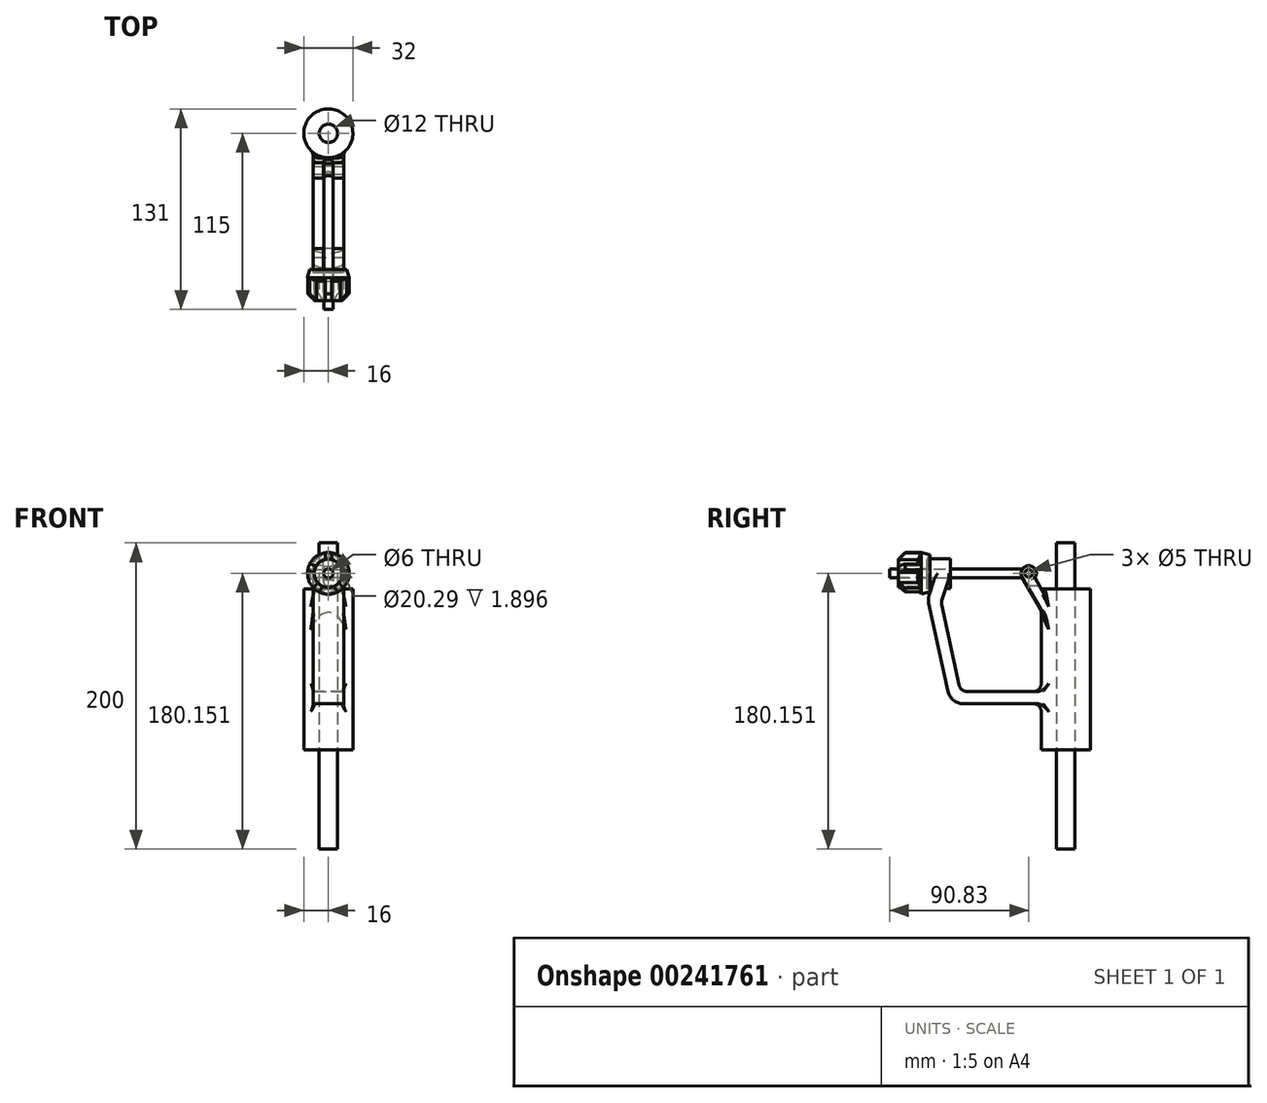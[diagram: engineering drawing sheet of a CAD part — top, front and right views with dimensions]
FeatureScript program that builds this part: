
annotation { "Feature Type Name" : "Feature", "Feature Type Description" : "" }
export const myFeature = defineFeature(function(context is Context, id is Id, definition is map)
    precondition{}
    {
        {
            var Q0;
            Q0=qCreatedBy(makeId("Top.planeOp"),FACE);
            var sketch = newSketch(context, id + "F0", { "sketchPlane" : qUnion([Q0])});
            skCircle(sketch, "E0", {"center": v(0, 0) * mm, "radius": 16 * mm});
            skCircle(sketch, "E1", {"center": v(0, 0) * mm, "radius": 6 * mm});
            skSolve(sketch);
        }
        {
            var Q0;
            Q0=makeQuery(id+"F0.imprint","IMPRINT",FACE,{"disambiguationData":[TD([[makeQuery(id+"F0.imprint","IMPRINT",EDGE,{"derivedFrom":sQuery(id+"F0.wireOp",EDGE,"E1")}),1.0]])]});
            extrude(context, id + "F1", {"entities" : qUnion([Q0]), "depth" : 135 * mm});
        }
        {
            var Q0;
            Q0=makeQuery(id+"F0.imprint","IMPRINT",FACE,{"disambiguationData":[TD([[makeQuery(id+"F0.imprint","IMPRINT",EDGE,{"derivedFrom":sQuery(id+"F0.wireOp",EDGE,"E1")}),1.0]])]});
            extrude(context, id + "F2", {"entities" : qUnion([Q0]), "operationType" : NewBodyOperationType.ADD, "oppositeDirection" : true, "depth" : 65 * mm});
        }
        {
            var Q0;
            Q0=makeQuery(id+"F0.imprint","IMPRINT",FACE,{"disambiguationData":[TD([[makeQuery(id+"F0.imprint","IMPRINT",EDGE,{"derivedFrom":sQuery(id+"F0.wireOp",EDGE,"E0")}),1.0]])]});
            extrude(context, id + "F3", {"entities" : qUnion([Q0]), "depth" : 105 * mm});
        }
        {
            var Q0;
            Q0=qCreatedBy(makeId("Right.planeOp"),FACE);
            var sketch = newSketch(context, id + "F4", { "sketchPlane" : qUnion([Q0])});
            skLineSegment(sketch, "E2", {"start": v(-16, 0) * mm, "end": v(-16, 30) * mm});
            skLineSegment(sketch, "E3", {"start": v(-16, 105) * mm, "end": v(-20.15, 112.18) * mm});
            skCircle(sketch, "E4", {"center": v(-24.17, 115.15) * mm, "radius": 5 * mm});
            skLineSegment(sketch, "E5", {"start": v(-28.5, 112.65) * mm, "end": v(-16, 91) * mm});
            skLineSegment(sketch, "E6", {"start": v(-7, 30) * mm, "end": v(-75, 30) * mm});
            skLineSegment(sketch, "E7", {"start": v(-75, 30) * mm, "end": v(-90, 98.37) * mm});
            skLineSegment(sketch, "E8", {"start": v(-90, 98.37) * mm, "end": v(-84.67, 115.15) * mm});
            skLineSegment(sketch, "E9", {"start": v(-84.67, 115.15) * mm, "end": v(-75.23, 115.15) * mm});
            skLineSegment(sketch, "E10", {"start": v(-75.23, 115.15) * mm, "end": v(-81.3, 96.04) * mm});
            skLineSegment(sketch, "E11", {"start": v(-81.3, 96.04) * mm, "end": v(-68.56, 38) * mm});
            skLineSegment(sketch, "E12", {"start": v(-68.56, 38) * mm, "end": v(-7, 38) * mm});
            skLineSegment(sketch, "E13", {"start": v(-16, 91) * mm, "end": v(-11.45, 83.12) * mm});
            skLineSegment(sketch, "E14", {"start": v(-11.45, 83.12) * mm, "end": v(-11.45, 97.12) * mm});
            skLineSegment(sketch, "E15", {"start": v(-11.45, 97.12) * mm, "end": v(-16, 105) * mm});
            skLineSegment(sketch, "E16", {"start": v(-7, 38) * mm, "end": v(-7, 30) * mm});
            skLineSegment(sketch, "E17.trimOffspring", {"start": v(-16, 38) * mm, "end": v(-16, 105) * mm});
            skSolve(sketch);
        }
        {
            var Q0;
            {var subQ0=sQuery(id+"F4.wireOp",EDGE,"E6");Q0=makeQuery(id+"F4.imprint","IMPRINT",FACE,{"disambiguationData":[TD([[makeQuery(id+"F4.imprint","IMPRINT",EDGE,{"derivedFrom":subQ0}),-1.0]])]});}
            var Q1;
            {var subQ0=sQuery(id+"F4.wireOp",EDGE,"E3");Q1=makeQuery(id+"F4.imprint","IMPRINT",FACE,{"disambiguationData":[TD([[makeQuery(id+"F4.imprint","IMPRINT",EDGE,{"derivedFrom":subQ0}),1.0]])]});}
            var Q2;
            {var subQ0=sQuery(id+"F4.wireOp",EDGE,"E4");var subQ1=makeQuery(id+"F4.imprint","INTERSECT",VERTEX,{"derivedFrom":[sQuery(id+"F4.wireOp",EDGE,"E3"),subQ0]});Q2=makeQuery(id+"F4.imprint","IMPRINT",FACE,{"disambiguationData":[TD([[makeQuery(id+"F4.imprint","IMPRINT",EDGE,{"disambiguationData":[TD([[subQ1,1.0]])],"derivedFrom":subQ0}),1.0]])]});}
            var Q3;
            {var subQ2=sQuery(id+"F4.wireOp",EDGE,"E13");Q3=makeQuery(id+"F4.imprint","IMPRINT",FACE,{"disambiguationData":[TD([[makeQuery(id+"F4.imprint","IMPRINT",EDGE,{"derivedFrom":subQ2}),1.0]])]});}
            extrude(context, id + "F5", {"entities" : qUnion([Q0, Q1, Q2, Q3]), "operationType" : NewBodyOperationType.ADD, "endBound" : BoundingType.SYMMETRIC, "depth" : 20 * mm});
        }
        {
            var Q0;
            Q0=qCreatedBy(makeId("Front.planeOp"),FACE);
            var Q1;
            Q1=sQuery(id+"F4.wireOp",VERTEX,"E9.start");
            cPlane(context, id + "F6", {"entities" : qUnion([Q0, Q1]), "cplaneType" : CPlaneType.PLANE_POINT, "offset" : 25 * mm, "width" : 150 * mm, "height" : 150 * mm});
        }
        {
            var Q0;
            Q0=qCreatedBy(id+"F6.planeOp",FACE);
            var sketch = newSketch(context, id + "F7", { "sketchPlane" : qUnion([Q0])});
            skPoint(sketch, "E18.0", {"position": v(0, 115.15) * mm});
            skArc(sketch, "E19", {"start": v(-3.25, 124.6) * mm, "mid": v(0, 105.15) * mm, "end": v(3.25, 124.6) * mm});
            skArc(sketch, "E20", {"start": v(-3.25, 115.15) * mm, "mid": v(0, 111.9) * mm, "end": v(3.25, 115.15) * mm});
            skLineSegment(sketch, "E21.left", {"start": v(-3.25, 115.15) * mm, "end": v(-3.25, 124.6) * mm});
            skLineSegment(sketch, "E21.right", {"start": v(3.25, 115.15) * mm, "end": v(3.25, 124.6) * mm});
            skSolve(sketch);
        }
        {
            var Q0;
            Q0=makeQuery(id+"F7.imprint","IMPRINT",FACE,{"disambiguationData":[TD([[makeQuery(id+"F7.imprint","IMPRINT",EDGE,{"derivedFrom":sQuery(id+"F7.wireOp",EDGE,"E19")}),1.0]])]});
            var Q1;
            Q1=sQuery(id+"F4.wireOp",VERTEX,"E10.start");
            extrude(context, id + "F8", {"entities" : qUnion([Q0]), "operationType" : NewBodyOperationType.ADD, "endBound" : BoundingType.UP_TO_VERTEX, "oppositeDirection" : true, "endBoundEntityVertex" : qUnion([Q1]), "depth" : 25 * mm});
        }
        {
            var Q0;
            Q0 = qSketchRegion(id + "F7", true);
            extrude(context, id + "F9", {"entities" : qUnion([Q0]), "operationType" : NewBodyOperationType.ADD, "depth" : 6 * mm});
        }
        {
            var Q0;
            Q0=makeQuery(id+"F9.opExtrude","CAP_FACE",FACE,{"disambiguationData":[OSD([sQuery(id+"F7.wireOp",EDGE,"E19"),sQuery(id+"F7.wireOp",EDGE,"E20"),sQuery(id+"F7.wireOp",EDGE,"E21.left"),sQuery(id+"F7.wireOp",EDGE,"E21.right")])],"isStart":false});
            var sketch = newSketch(context, id + "F10", { "sketchPlane" : qUnion([Q0])});
            skCircle(sketch, "E22", {"center": v(0, 115.15) * mm, "radius": 3.25 * mm});
            skLineSegment(sketch, "E23.bottom", {"start": v(-3.25, 115.15) * mm, "end": v(3.25, 115.15) * mm});
            skLineSegment(sketch, "E23.top", {"start": v(-3.25, 124.6) * mm, "end": v(3.25, 124.6) * mm});
            skLineSegment(sketch, "E23.left", {"start": v(-3.25, 115.15) * mm, "end": v(-3.25, 124.6) * mm});
            skLineSegment(sketch, "E23.right", {"start": v(3.25, 115.15) * mm, "end": v(3.25, 124.6) * mm});
            skSolve(sketch);
        }
        {
            var Q0;
            Q0 = qSketchRegion(id + "F10", true);
            extrude(context, id + "F11", {"entities" : qUnion([Q0]), "operationType" : NewBodyOperationType.REMOVE, "oppositeDirection" : true, "depth" : 30 * mm});
        }
        {
            var Q0;
            Q0=qCreatedBy(makeId("Front.planeOp"),FACE);
            cPlane(context, id + "F12", {"entities" : qUnion([Q0]), "cplaneType" : CPlaneType.OFFSET, "offset" : 40 * mm, "width" : 150 * mm, "height" : 150 * mm});
        }
        {
            var Q0;
            Q0=qCreatedBy(id+"F12.planeOp",FACE);
            var sketch = newSketch(context, id + "F13", { "sketchPlane" : qUnion([Q0])});
            skCircle(sketch, "E24", {"center": v(0, 110.14) * mm, "radius": 3.25 * mm});
            skLineSegment(sketch, "E25.bottom", {"start": v(-3.25, 110.14) * mm, "end": v(3.25, 110.14) * mm});
            skLineSegment(sketch, "E25.top", {"start": v(-3.25, 124.6) * mm, "end": v(3.25, 124.6) * mm});
            skLineSegment(sketch, "E25.left", {"start": v(-3.25, 110.14) * mm, "end": v(-3.25, 124.6) * mm});
            skLineSegment(sketch, "E25.right", {"start": v(3.25, 110.14) * mm, "end": v(3.25, 124.6) * mm});
            skSolve(sketch);
        }
        {
            var Q0;
            Q0=makeQuery(id+"F13.imprint","IMPRINT",FACE,{"disambiguationData":[TD([[makeQuery(id+"F13.imprint","IMPRINT",EDGE,{"derivedFrom":sQuery(id+"F13.wireOp",EDGE,"E25.top")}),-1.0]])]});
            var Q1;
            {var subQ0=sQuery(id+"F13.wireOp",EDGE,"E25.bottom");Q1=makeQuery(id+"F13.imprint","IMPRINT",FACE,{"disambiguationData":[TD([[makeQuery(id+"F13.imprint","IMPRINT",EDGE,{"derivedFrom":subQ0}),1.0]])]});}
            var Q2;
            {var subQ0=sQuery(id+"F13.wireOp",EDGE,"E25.bottom");Q2=makeQuery(id+"F13.imprint","IMPRINT",FACE,{"disambiguationData":[TD([[makeQuery(id+"F13.imprint","IMPRINT",EDGE,{"derivedFrom":subQ0}),-1.0]])]});}
            extrude(context, id + "F14", {"entities" : qUnion([Q0, Q1, Q2]), "operationType" : NewBodyOperationType.REMOVE, "oppositeDirection" : true, "depth" : 25 * mm});
        }
        {
            var Q0;
            Q0=qCreatedBy(makeId("Right.planeOp"),FACE);
            var sketch = newSketch(context, id + "F15", { "sketchPlane" : qUnion([Q0])});
            skPoint(sketch, "E26.0", {"position": v(-24.17, 115.15) * mm});
            skCircle(sketch, "E27", {"center": v(-24.17, 115.15) * mm, "radius": 2.5 * mm});
            skCircle(sketch, "E28", {"center": v(-24.17, 115.15) * mm, "radius": 4.5 * mm});
            skSolve(sketch);
        }
        {
            var Q0;
            Q0=makeQuery(id+"F15.imprint","IMPRINT",FACE,{"disambiguationData":[TD([[makeQuery(id+"F15.imprint","IMPRINT",EDGE,{"derivedFrom":sQuery(id+"F15.wireOp",EDGE,"E27")}),-1.0]])]});
            extrude(context, id + "F16", {"entities" : qUnion([Q0]), "endBound" : BoundingType.SYMMETRIC, "depth" : 6 * mm});
        }
        {
            var Q0;
            Q0=qCreatedBy(makeId("Front.planeOp"),FACE);
            var Q1;
            Q1=sQuery(id+"F4.wireOp",VERTEX,"E4.center");
            cPlane(context, id + "F17", {"entities" : qUnion([Q0, Q1]), "cplaneType" : CPlaneType.PLANE_POINT, "offset" : 25 * mm, "width" : 150 * mm, "height" : 150 * mm});
        }
        {
            var Q0;
            Q0=qCreatedBy(id+"F17.planeOp",FACE);
            var sketch = newSketch(context, id + "F18", { "sketchPlane" : qUnion([Q0])});
            skPoint(sketch, "E29.0", {"position": v(0, 115.15) * mm});
            skCircle(sketch, "E30", {"center": v(0, 115.15) * mm, "radius": 3 * mm});
            skSolve(sketch);
        }
        {
            var Q0;
            Q0=qCreatedBy(makeId("Front.planeOp"),FACE);
            cPlane(context, id + "F19", {"entities" : qUnion([Q0]), "cplaneType" : CPlaneType.OFFSET, "offset" : 115 * mm, "width" : 150 * mm, "height" : 150 * mm});
        }
        {
            var Q0;
            Q0 = qSketchRegion(id + "F18", true);
            var Q1;
            Q1=qCreatedBy(id+"F19.planeOp",FACE);
            extrude(context, id + "F20", {"entities" : qUnion([Q0]), "operationType" : NewBodyOperationType.ADD, "endBound" : BoundingType.UP_TO_SURFACE, "endBoundEntityFace" : qUnion([Q1]), "depth" : 90 * mm});
        }
        {
            var Q0;
            Q0=makeQuery(id+"F5.opExtrude","CAP_FACE",FACE,{"disambiguationData":[OSD([sQuery(id+"F4.wireOp",EDGE,"E3"),sQuery(id+"F4.wireOp",EDGE,"E4"),sQuery(id+"F4.wireOp",EDGE,"E5"),sQuery(id+"F4.wireOp",EDGE,"E13"),sQuery(id+"F4.wireOp",EDGE,"E14"),sQuery(id+"F4.wireOp",EDGE,"E15")])],"isStart":false});
            var sketch = newSketch(context, id + "F21", { "sketchPlane" : qUnion([Q0])});
            skCircle(sketch, "E31", {"center": v(-24.17, 115.15) * mm, "radius": 2.5 * mm});
            skSolve(sketch);
        }
        {
            var Q0;
            Q0=makeQuery(id+"F21.imprint","IMPRINT",FACE,{"disambiguationData":[TD([[makeQuery(id+"F21.imprint","IMPRINT",EDGE,{"derivedFrom":sQuery(id+"F21.wireOp",EDGE,"E31")}),1.0]])]});
            extrude(context, id + "F22", {"entities" : qUnion([Q0]), "operationType" : NewBodyOperationType.REMOVE, "oppositeDirection" : true, "depth" : 25 * mm});
        }
        {
            var Q0;
            Q0=qCreatedBy(makeId("Right.planeOp"),FACE);
            var sketch = newSketch(context, id + "F23", { "sketchPlane" : qUnion([Q0])});
            skLineSegment(sketch, "E32", {"start": v(-109.11, 118.15) * mm, "end": v(-90.65, 118.15) * mm});
            skLineSegment(sketch, "E33", {"start": v(-109.11, 118.15) * mm, "end": v(-109.11, 124.34) * mm});
            skLineSegment(sketch, "E34", {"start": v(-94.44, 128.76) * mm, "end": v(-88.76, 127.18) * mm});
            skLineSegment(sketch, "E35", {"start": v(-88.76, 127.18) * mm, "end": v(-88.76, 125.3) * mm});
            skLineSegment(sketch, "E36", {"start": v(-88.76, 125.3) * mm, "end": v(-90.65, 125.3) * mm});
            skLineSegment(sketch, "E37", {"start": v(-90.65, 125.3) * mm, "end": v(-90.65, 118.15) * mm});
            skLineSegment(sketch, "E38", {"start": v(-94.44, 128.76) * mm, "end": v(-96.4, 124.34) * mm});
            skLineSegment(sketch, "E39", {"start": v(-96.4, 124.34) * mm, "end": v(-109.11, 124.34) * mm});
            skSolve(sketch);
        }
        {
            var Q0;
            Q0=makeQuery(id+"F23.imprint","IMPRINT",FACE,{"disambiguationData":[TD([[makeQuery(id+"F23.imprint","IMPRINT",EDGE,{"derivedFrom":sQuery(id+"F23.wireOp",EDGE,"E32")}),1.0]])]});
            var Q1;
            {var subQ0=sQuery(id+"F15.wireOp",EDGE,"E28");var subQ1=sQuery(id+"F15.wireOp",EDGE,"E27");Q1=makeQuery(id+"F20.boolean.opBoolean","SPLIT",FACE,{"disambiguationData":[TD([makeQuery(id+"F16.opExtrude","CAP_FACE",FACE,{"disambiguationData":[OSD([subQ1,subQ0])],"isStart":true}),makeQuery(id+"F16.opExtrude","CAP_FACE",FACE,{"disambiguationData":[OSD([subQ1,subQ0])],"isStart":false}),makeQuery(id+"F16.opExtrude","SWEPT_FACE",FACE,{"disambiguationData":[OSD([subQ0])]}),makeQuery(id+"F20.opExtrude","CAP_FACE",FACE,{"disambiguationData":[OSD([dummyQuery(id+"F19.planeOp",FACE)])],"isStart":false})])],"derivedFrom":makeQuery(id+"F20.opExtrude","SWEPT_FACE",FACE,{"disambiguationData":[OSD([sQuery(id+"F18.wireOp",EDGE,"E30")])]})});}
            revolve(context, id + "F24", {"entities" : qUnion([Q0]), "axis" : qUnion([Q1]), "revolveType" : RevolveType.FULL});
        }
        {
            var Q0;
            Q0=makeQuery(id+"F24.opRevolve","SWEPT_FACE",FACE,{"disambiguationData":[OSD([sQuery(id+"F23.wireOp",EDGE,"E33")])]});
            var sketch = newSketch(context, id + "F25", { "sketchPlane" : qUnion([Q0])});
            skArc(sketch, "E40.0", {"start": v(2.13, 128.59) * mm, "mid": v(0, 128.76) * mm, "end": v(-2.13, 128.59) * mm});
            skArc(sketch, "E41.0", {"start": v(-7.84, 119.94) * mm, "mid": v(-8.74, 117.99) * mm, "end": v(-9.16, 115.89) * mm});
            skLineSegment(sketch, "E42", {"start": v(-2.13, 128.59) * mm, "end": v(-2.13, 124.09) * mm});
            skLineSegment(sketch, "E43.MirrorCS", {"start": v(2.13, 128.59) * mm, "end": v(2.13, 124.09) * mm});
            skLineSegment(sketch, "E44.1.0", {"start": v(-12.12, 121.33) * mm, "end": v(-7.84, 119.94) * mm});
            skLineSegment(sketch, "E44.1.1", {"start": v(-13.44, 117.28) * mm, "end": v(-9.16, 115.89) * mm});
            skLineSegment(sketch, "E44.2.0", {"start": v(-9.62, 105.53) * mm, "end": v(-6.97, 109.17) * mm});
            skLineSegment(sketch, "E44.2.1", {"start": v(-6.18, 103.03) * mm, "end": v(-3.53, 106.67) * mm});
            skLineSegment(sketch, "E44.3.0", {"start": v(6.18, 103.03) * mm, "end": v(3.53, 106.67) * mm});
            skLineSegment(sketch, "E44.3.1", {"start": v(9.62, 105.53) * mm, "end": v(6.97, 109.17) * mm});
            skLineSegment(sketch, "E44.4.0", {"start": v(13.44, 117.28) * mm, "end": v(9.16, 115.89) * mm});
            skLineSegment(sketch, "E44.4.1", {"start": v(12.12, 121.33) * mm, "end": v(7.84, 119.94) * mm});
            skLineSegment(sketch, "E45", {"start": v(0, 115.15) * mm, "end": v(0, 121.16) * mm, "construction": true});
            skArc(sketch, "E46.trimOffspring", {"start": v(-12.12, 121.33) * mm, "mid": v(-12.94, 119.35) * mm, "end": v(-13.44, 117.28) * mm});
            skArc(sketch, "E47.trimOffspring", {"start": v(2.13, 124.09) * mm, "mid": v(0, 124.34) * mm, "end": v(-2.13, 124.09) * mm});
            skArc(sketch, "E48.trimOffspring", {"start": v(-9.62, 105.53) * mm, "mid": v(-8, 104.14) * mm, "end": v(-6.18, 103.03) * mm});
            skArc(sketch, "E49.trimOffspring", {"start": v(-6.97, 109.17) * mm, "mid": v(-5.4, 107.72) * mm, "end": v(-3.53, 106.67) * mm});
            skArc(sketch, "E50.trimOffspring", {"start": v(9.16, 115.89) * mm, "mid": v(8.74, 117.99) * mm, "end": v(7.84, 119.94) * mm});
            skArc(sketch, "E51.trimOffspring", {"start": v(3.53, 106.67) * mm, "mid": v(5.4, 107.72) * mm, "end": v(6.97, 109.17) * mm});
            skArc(sketch, "E52.trimOffspring", {"start": v(13.44, 117.28) * mm, "mid": v(12.94, 119.35) * mm, "end": v(12.12, 121.33) * mm});
            skArc(sketch, "E53.trimOffspring", {"start": v(6.18, 103.03) * mm, "mid": v(8, 104.14) * mm, "end": v(9.62, 105.53) * mm});
            skSolve(sketch);
        }
        {
            var Q0;
            Q0=makeQuery(id+"F25.imprint","IMPRINT",FACE,{"disambiguationData":[TD([[makeQuery(id+"F25.imprint","IMPRINT",EDGE,{"derivedFrom":sQuery(id+"F25.wireOp",EDGE,"E40.0")}),1.0]])]});
            var Q1;
            Q1=makeQuery(id+"F25.imprint","IMPRINT",FACE,{"disambiguationData":[TD([[makeQuery(id+"F25.imprint","IMPRINT",EDGE,{"derivedFrom":sQuery(id+"F25.wireOp",EDGE,"E44.4.0")}),-1.0]])]});
            var Q2;
            Q2=makeQuery(id+"F25.imprint","IMPRINT",FACE,{"disambiguationData":[TD([[makeQuery(id+"F25.imprint","IMPRINT",EDGE,{"derivedFrom":sQuery(id+"F25.wireOp",EDGE,"E44.3.0")}),-1.0]])]});
            var Q3;
            Q3=makeQuery(id+"F25.imprint","IMPRINT",FACE,{"disambiguationData":[TD([[makeQuery(id+"F25.imprint","IMPRINT",EDGE,{"derivedFrom":sQuery(id+"F25.wireOp",EDGE,"E44.2.0")}),-1.0]])]});
            var Q4;
            Q4=makeQuery(id+"F25.imprint","IMPRINT",FACE,{"disambiguationData":[TD([[makeQuery(id+"F25.imprint","IMPRINT",EDGE,{"derivedFrom":sQuery(id+"F25.wireOp",EDGE,"E41.0")}),-1.0]])]});
            extrude(context, id + "F26", {"entities" : qUnion([Q0, Q1, Q2, Q3, Q4]), "operationType" : NewBodyOperationType.ADD, "endBound" : BoundingType.UP_TO_NEXT, "oppositeDirection" : true, "depth" : 25 * mm});
        }
        {
            var Q0;
            Q0=qCreatedBy(makeId("Right.planeOp"),FACE);
            var sketch = newSketch(context, id + "F27", { "sketchPlane" : qUnion([Q0])});
            skPoint(sketch, "E54.0", {"position": v(-109.11, 105.96) * mm});
            skLineSegment(sketch, "E55", {"start": v(-109.11, 105.96) * mm, "end": v(-102.04, 98.9) * mm});
            skLineSegment(sketch, "E56", {"start": v(-102.04, 98.9) * mm, "end": v(-109.11, 98.9) * mm});
            skLineSegment(sketch, "E57", {"start": v(-109.11, 98.9) * mm, "end": v(-109.11, 105.96) * mm});
            skSolve(sketch);
        }
        {
            var Q0;
            Q0=makeQuery(id+"F27.imprint","IMPRINT",FACE,{"disambiguationData":[TD([[makeQuery(id+"F27.imprint","IMPRINT",EDGE,{"derivedFrom":sQuery(id+"F27.wireOp",EDGE,"E55")}),-1.0]])]});
            var Q1;
            {var subQ0=sQuery(id+"F25.wireOp",EDGE,"E44.3.1");Q1=makeQuery(id+"F26.boolean.opBoolean","SPLIT",FACE,{"disambiguationData":[TD([makeQuery(id+"F26.opExtrude","SWEPT_FACE",FACE,{"disambiguationData":[OSD([subQ0])]})])],"derivedFrom":makeQuery(id+"F24.opRevolve","SWEPT_FACE",FACE,{"disambiguationData":[OSD([sQuery(id+"F23.wireOp",EDGE,"E39")])]})});}
            revolve(context, id + "F28", {"operationType" : NewBodyOperationType.REMOVE, "entities" : qUnion([Q0]), "axis" : qUnion([Q1]), "revolveType" : RevolveType.FULL, "oppositeDirection" : true});
        }
        {
            var Q0;
            Q0=makeQuery(id+"F5.opExtrude","SWEPT_EDGE",EDGE,{"disambiguationData":[OSD([sQuery(id+"F4.wireOp",EDGE,"E11"),sQuery(id+"F4.wireOp",EDGE,"E12")])]});
            var Q1;
            Q1=makeQuery(id+"F5.opExtrude","SWEPT_EDGE",EDGE,{"disambiguationData":[OSD([sQuery(id+"F4.wireOp",EDGE,"E10"),sQuery(id+"F4.wireOp",EDGE,"E11")])]});
            var Q2;
            Q2=makeQuery(id+"F5.boolean.opBoolean","INTERSECT",EDGE,{"derivedFrom":[makeQuery(id+"F3.opExtrude","SWEPT_FACE",FACE,{"disambiguationData":[OSD([sQuery(id+"F0.wireOp",EDGE,"E0")])]}),makeQuery(id+"F5.opExtrude","SWEPT_FACE",FACE,{"disambiguationData":[OSD([sQuery(id+"F4.wireOp",EDGE,"E12")])]})]});
            var Q3;
            Q3=makeQuery(id+"F5.boolean.opBoolean","INTERSECT",EDGE,{"derivedFrom":[makeQuery(id+"F3.opExtrude","SWEPT_FACE",FACE,{"disambiguationData":[OSD([sQuery(id+"F0.wireOp",EDGE,"E0")])]}),makeQuery(id+"F5.opExtrude","CAP_FACE",FACE,{"disambiguationData":[OSD([sQuery(id+"F4.wireOp",EDGE,"E6"),sQuery(id+"F4.wireOp",EDGE,"E7"),sQuery(id+"F4.wireOp",EDGE,"E8"),sQuery(id+"F4.wireOp",EDGE,"E9"),sQuery(id+"F4.wireOp",EDGE,"E10"),sQuery(id+"F4.wireOp",EDGE,"E11"),sQuery(id+"F4.wireOp",EDGE,"E12"),sQuery(id+"F4.wireOp",EDGE,"E16")])],"isStart":false})]});
            var Q4;
            Q4=makeQuery(id+"F5.boolean.opBoolean","INTERSECT",EDGE,{"derivedFrom":[makeQuery(id+"F3.opExtrude","SWEPT_FACE",FACE,{"disambiguationData":[OSD([sQuery(id+"F0.wireOp",EDGE,"E0")])]}),makeQuery(id+"F5.opExtrude","SWEPT_FACE",FACE,{"disambiguationData":[OSD([sQuery(id+"F4.wireOp",EDGE,"E6")])]})]});
            var Q5;
            Q5=makeQuery(id+"F5.boolean.opBoolean","INTERSECT",EDGE,{"derivedFrom":[makeQuery(id+"F3.opExtrude","SWEPT_FACE",FACE,{"disambiguationData":[OSD([sQuery(id+"F0.wireOp",EDGE,"E0")])]}),makeQuery(id+"F5.opExtrude","CAP_FACE",FACE,{"disambiguationData":[OSD([sQuery(id+"F4.wireOp",EDGE,"E6"),sQuery(id+"F4.wireOp",EDGE,"E7"),sQuery(id+"F4.wireOp",EDGE,"E8"),sQuery(id+"F4.wireOp",EDGE,"E9"),sQuery(id+"F4.wireOp",EDGE,"E10"),sQuery(id+"F4.wireOp",EDGE,"E11"),sQuery(id+"F4.wireOp",EDGE,"E12"),sQuery(id+"F4.wireOp",EDGE,"E16")])],"isStart":true})]});
            var Q6;
            Q6=makeQuery(id+"F5.boolean.opBoolean","INTERSECT",EDGE,{"derivedFrom":[makeQuery(id+"F3.opExtrude","SWEPT_FACE",FACE,{"disambiguationData":[OSD([sQuery(id+"F0.wireOp",EDGE,"E0")])]}),makeQuery(id+"F5.opExtrude","SWEPT_FACE",FACE,{"disambiguationData":[OSD([sQuery(id+"F4.wireOp",EDGE,"E5"),sQuery(id+"F4.wireOp",EDGE,"E13")])]})]});
            var Q7;
            Q7=makeQuery(id+"F5.boolean.opBoolean","INTERSECT",EDGE,{"derivedFrom":[makeQuery(id+"F3.opExtrude","SWEPT_FACE",FACE,{"disambiguationData":[OSD([sQuery(id+"F0.wireOp",EDGE,"E0")])]}),makeQuery(id+"F5.opExtrude","CAP_FACE",FACE,{"disambiguationData":[OSD([sQuery(id+"F4.wireOp",EDGE,"E3"),sQuery(id+"F4.wireOp",EDGE,"E4"),sQuery(id+"F4.wireOp",EDGE,"E5"),sQuery(id+"F4.wireOp",EDGE,"E13"),sQuery(id+"F4.wireOp",EDGE,"E14"),sQuery(id+"F4.wireOp",EDGE,"E15")])],"isStart":true})]});
            var Q8;
            Q8=makeQuery(id+"F5.boolean.opBoolean","INTERSECT",EDGE,{"derivedFrom":[makeQuery(id+"F3.opExtrude","SWEPT_FACE",FACE,{"disambiguationData":[OSD([sQuery(id+"F0.wireOp",EDGE,"E0")])]}),makeQuery(id+"F5.opExtrude","CAP_FACE",FACE,{"disambiguationData":[OSD([sQuery(id+"F4.wireOp",EDGE,"E3"),sQuery(id+"F4.wireOp",EDGE,"E4"),sQuery(id+"F4.wireOp",EDGE,"E5"),sQuery(id+"F4.wireOp",EDGE,"E13"),sQuery(id+"F4.wireOp",EDGE,"E14"),sQuery(id+"F4.wireOp",EDGE,"E15")])],"isStart":false})]});
            fillet(context, id + "F29", {"entities" : qUnion([Q0, Q1, Q2, Q3, Q4, Q5, Q6, Q7, Q8]), "radius" : 5 * mm, "tangentPropagation" : true, "allowEdgeOverflow" : false});
        }
        {
            var Q0;
            Q0=makeQuery(id+"F5.opExtrude","SWEPT_EDGE",EDGE,{"disambiguationData":[OSD([sQuery(id+"F4.wireOp",EDGE,"E6"),sQuery(id+"F4.wireOp",EDGE,"E7")])]});
            var Q1;
            Q1=makeQuery(id+"F5.opExtrude","SWEPT_EDGE",EDGE,{"disambiguationData":[OSD([sQuery(id+"F4.wireOp",EDGE,"E7"),sQuery(id+"F4.wireOp",EDGE,"E8")])]});
            fillet(context, id + "F30", {"entities" : qUnion([Q0, Q1]), "radius" : 10 * mm, "tangentPropagation" : true, "allowEdgeOverflow" : false});
        }
        {
            var Q0;
            Q0=makeQuery(id+"F5.opExtrude","CAP_EDGE",EDGE,{"disambiguationData":[OSD([sQuery(id+"F4.wireOp",EDGE,"E3"),sQuery(id+"F4.wireOp",EDGE,"E15")])],"isStart":false});
            var Q1;
            Q1=makeQuery(id+"F5.opExtrude","CAP_EDGE",EDGE,{"disambiguationData":[OSD([sQuery(id+"F4.wireOp",EDGE,"E4")])],"isStart":false});
            var Q2;
            Q2=makeQuery(id+"F5.opExtrude","CAP_EDGE",EDGE,{"disambiguationData":[OSD([sQuery(id+"F4.wireOp",EDGE,"E5"),sQuery(id+"F4.wireOp",EDGE,"E13")])],"isStart":true});
            var Q3;
            Q3=makeQuery(id+"F5.opExtrude","CAP_EDGE",EDGE,{"disambiguationData":[OSD([sQuery(id+"F4.wireOp",EDGE,"E3"),sQuery(id+"F4.wireOp",EDGE,"E15")])],"isStart":true});
            var Q4;
            Q4=makeQuery(id+"F5.boolean.opBoolean","INTERSECT",EDGE,{"disambiguationData":[OD(0.0)],"derivedFrom":[makeQuery(id+"F3.opExtrude","SWEPT_FACE",FACE,{"disambiguationData":[OSD([sQuery(id+"F0.wireOp",EDGE,"E0")])]}),makeQuery(id+"F5.opExtrude","SWEPT_FACE",FACE,{"disambiguationData":[OSD([sQuery(id+"F4.wireOp",EDGE,"E3"),sQuery(id+"F4.wireOp",EDGE,"E15")])]})]});
            fillet(context, id + "F31", {"entities" : qUnion([Q0, Q1, Q2, Q3, Q4]), "radius" : 1 * mm, "tangentPropagation" : true, "allowEdgeOverflow" : false});
        }
        {
            var Q0;
            Q0=makeQuery(id+"F5.opExtrude","CAP_FACE",FACE,{"disambiguationData":[OSD([sQuery(id+"F4.wireOp",EDGE,"E6"),sQuery(id+"F4.wireOp",EDGE,"E7"),sQuery(id+"F4.wireOp",EDGE,"E8"),sQuery(id+"F4.wireOp",EDGE,"E9"),sQuery(id+"F4.wireOp",EDGE,"E10"),sQuery(id+"F4.wireOp",EDGE,"E11"),sQuery(id+"F4.wireOp",EDGE,"E12"),sQuery(id+"F4.wireOp",EDGE,"E16")])],"isStart":false});
            fillet(context, id + "F32", {"entities" : qUnion([Q0]), "radius" : 1 * mm, "tangentPropagation" : true, "allowEdgeOverflow" : false});
        }
        {
            var Q0;
            Q0=makeQuery(id+"F5.opExtrude","CAP_FACE",FACE,{"disambiguationData":[OSD([sQuery(id+"F4.wireOp",EDGE,"E6"),sQuery(id+"F4.wireOp",EDGE,"E7"),sQuery(id+"F4.wireOp",EDGE,"E8"),sQuery(id+"F4.wireOp",EDGE,"E9"),sQuery(id+"F4.wireOp",EDGE,"E10"),sQuery(id+"F4.wireOp",EDGE,"E11"),sQuery(id+"F4.wireOp",EDGE,"E12"),sQuery(id+"F4.wireOp",EDGE,"E16")])],"isStart":true});
            fillet(context, id + "F33", {"entities" : qUnion([Q0]), "radius" : 1 * mm, "tangentPropagation" : true, "allowEdgeOverflow" : false});
        }
        {
            var Q0;
            Q0=makeQuery(id+"F5.opExtrude","CAP_FACE",FACE,{"disambiguationData":[OSD([sQuery(id+"F4.wireOp",EDGE,"E3"),sQuery(id+"F4.wireOp",EDGE,"E4"),sQuery(id+"F4.wireOp",EDGE,"E5"),sQuery(id+"F4.wireOp",EDGE,"E13"),sQuery(id+"F4.wireOp",EDGE,"E14"),sQuery(id+"F4.wireOp",EDGE,"E15")])],"isStart":false});
            var sketch = newSketch(context, id + "F34", { "sketchPlane" : qUnion([Q0])});
            skCircle(sketch, "E58.0", {"center": v(-24.17, 115.15) * mm, "radius": 2.5 * mm});
            skSolve(sketch);
        }
        {
            var Q0;
            Q0=makeQuery(id+"F34.imprint","IMPRINT",FACE,{"disambiguationData":[TD([[makeQuery(id+"F34.imprint","IMPRINT",EDGE,{"derivedFrom":sQuery(id+"F34.wireOp",EDGE,"E58.0")}),1.0]])]});
            var Q1;
            Q1=makeQuery(id+"F5.opExtrude","CAP_FACE",FACE,{"disambiguationData":[OSD([sQuery(id+"F4.wireOp",EDGE,"E3"),sQuery(id+"F4.wireOp",EDGE,"E4"),sQuery(id+"F4.wireOp",EDGE,"E5"),sQuery(id+"F4.wireOp",EDGE,"E13"),sQuery(id+"F4.wireOp",EDGE,"E14"),sQuery(id+"F4.wireOp",EDGE,"E15")])],"isStart":true});
            extrude(context, id + "F35", {"entities" : qUnion([Q0]), "endBound" : BoundingType.UP_TO_SURFACE, "oppositeDirection" : true, "endBoundEntityFace" : qUnion([Q1]), "depth" : 25 * mm});
        }
    });
